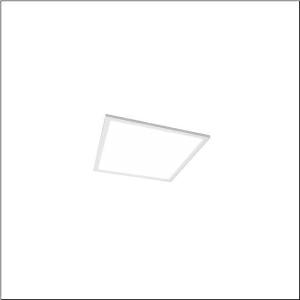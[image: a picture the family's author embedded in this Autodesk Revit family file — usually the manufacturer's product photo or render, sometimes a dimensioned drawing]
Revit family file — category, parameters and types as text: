
# Revit family: apollon_r__21_square_51mq13wd2313_d027
name_source: partatom
category: Lighting Fixtures
units: mm (PartAtom-declared; Revit-internal decimal feet)

## family parameters
Cut with Voids When Loaded = No
Host = Face
Light Source = No
Part Type = Normal
Room Calculation Point = No
Round Connector Dimension = Use Diameter
Shared = No

## types (1)
- Apollon® 21 square (1 x LED, 1700 lm, 15 W, 3000K)
    Apparent Load = 15 VA
    CIE Flux Codes = 59 88 97 100 100
    Color Rendering = 80
    Color Temperature = 3000K
    Default Elevation = 1800 mm
    Description = Apollon® 21 square, office luminaire, primary optical cover: micro prismatic cover, of PMMA, CAT 2 (L<= 3000cd/m²), light emission: direct distribution, primary light characteristic: symmetric, installation type: lay-in mounting, LED, rated luminous flux: 1.700lm, luminous efficacy: 113lm/W, light colour: 830, colour temperature: 3000K, control gear: ECG DALI, with terminal, 5-pole, mains connection: 220..240V, AC, 50/60Hz, rated input power: 15W, housing, of sheet steel, coated, pure white, length: 296mm, width: 296mm, height: 40mm, housing upper side, of sheet steel, galvanised, protection rating (complete): IP20, protection rating (lamp compartment, on room side): IP50, insulation class (complete): insulation class II (safety insulation), certification: CE, ENEC, permissible operating ambient temperature: -20..+40°C, packaging unit: 1 piece
    Height = 0 mm  [stored 0 ft]
    Lamp = 1 x LED
    Lamp Light Flux = 1700 lm
    Lamp Power = 15 W
    Lamp count = 1
    Length = 295 mm
    Luminous efficacy = 113 lm/W
    Manufacturer = Siteco
    ModVariant = No
    Model = 51MQ13WD2313
    Mounting Place = Ceiling
    Mounting Type = Recessed
    Number of Poles = 1
    OnlyDefault = Yes
    Power Factor = 1
    Product Name = Apollon® 21 square
    Product group = office luminaire | ceiling recessed
    ProductGroupID = 401
    Protection Class = Protection class II
    Protection Degree = IP 20
    RLX_Detail_Level = 1
    RLX_Emergency_Light_Flux = 0 lm
    RLX_Emergency_Type = 0
    RLX_Emergency_Type_DB = No
    RlxData = <blob elided: 10737 chars, md5=80273b34>
    Socket = socket
    Standby Power = 0 W
    System Light Flux = 1700 lm
    System Power = 15 W
    Type Comments = Product without accessories
    Type Image = l_1291030.jpg
    URL = http://relux.com
    VarID = ---
    Voltage = 0 V
    Weight = 0.00 kg
    Width = 295 mm

note: [stored X ft] marks values corroborated as IEEE doubles in the binary element streams (Revit-internal decimal feet)

## geometry (parser evidence)
native form markers: Sweep x8
no freeform markers — native parametric forms only
